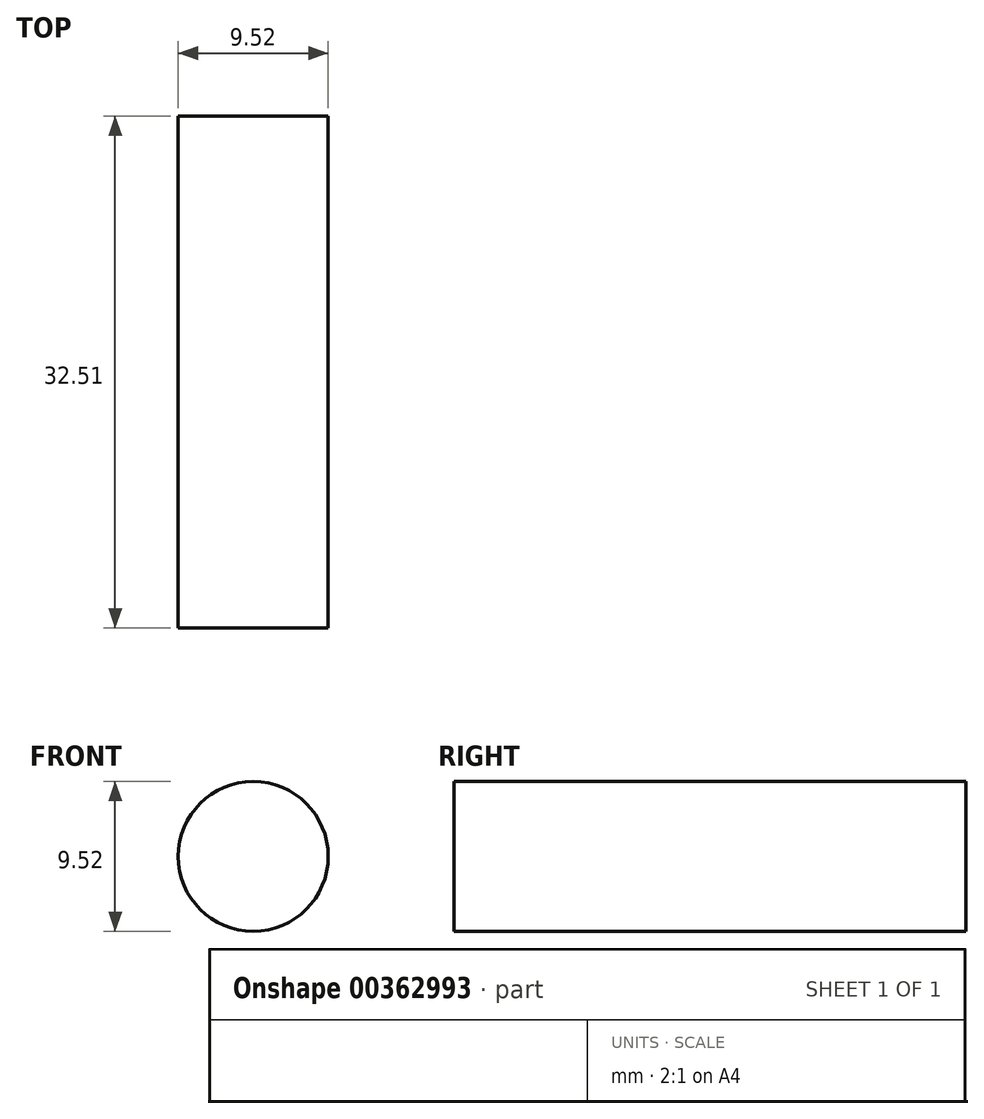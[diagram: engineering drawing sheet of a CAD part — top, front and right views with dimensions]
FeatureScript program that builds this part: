
annotation { "Feature Type Name" : "Feature", "Feature Type Description" : "" }
export const myFeature = defineFeature(function(context is Context, id is Id, definition is map)
    precondition{}
    {
        {
            var Q0;
            Q0=qCreatedBy(makeId("Front.planeOp"),FACE);
            var sketch = newSketch(context, id + "F0", { "sketchPlane" : qUnion([Q0])});
            skCircle(sketch, "E0", {"center": v(0, 0) * mm, "radius": 4.76 * mm});
            skSolve(sketch);
        }
        {
            var Q0;
            Q0=makeQuery(id+"F0.imprint","IMPRINT",FACE,{"disambiguationData":[TD([[makeQuery(id+"F0.imprint","IMPRINT",EDGE,{"derivedFrom":sQuery(id+"F0.wireOp",EDGE,"E0")}),1.0]])]});
            extrude(context, id + "F1", {"entities" : qUnion([Q0]), "depth" : 32.5 * mm});
        }
    });
